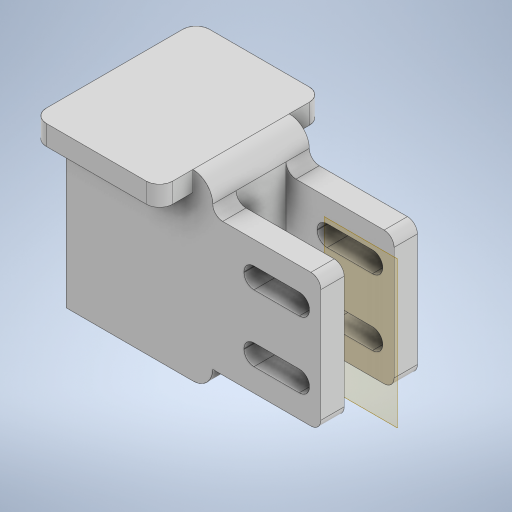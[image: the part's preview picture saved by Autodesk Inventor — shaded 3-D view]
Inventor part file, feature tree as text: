
AUTODESK INVENTOR PART (.ipt)
format: ipt  version: 2024 (Build 280153000, 153)  size: 822,784 bytes
history: native  units: mm
features: move_body x6, extrude x5, fillet x5, direct_edit x5, sketch x5, projected_geometry x5, other x2, plane x1, mirror x1, reference x1
ambient origin geometry x8: Origin, YZ Plane, XZ Plane, XY Plane, X Axis, Y Axis, Z Axis, Center Point
bodies: Solid1 (feature_tree)
feature tree (36):
  extrude  "Extrusion1"  Depth=20.0mm TaperAngle=0.0deg
  fillet  "Fillet1"  Radius=20.0mm
  plane  "Work Plane1"
  mirror  "Mirror1"
  fillet  "Fillet2"  [1 undecoded]
  extrude  "Extrusion2"  Depth=20.0mm
  fillet  "Fillet3"  Radius=10.0mm
  direct_edit  "Direct Edit1"
  extrude  "Extrusion3"  Depth=0.3mm
  direct_edit  "Direct Edit2"
  direct_edit  "Direct Edit3"
  direct_edit  "Direct Edit4"
  direct_edit  "Direct Edit5"
  extrude  "Extrusion4"  Depth=1.5mm
  fillet  "Fillet4"  Radius=1.5mm
  extrude  "Extrusion5"  Depth=20.0mm
  fillet  "Fillet5"  Radius=4.0mm
  sketch  "Sketch2"  dims[d0=40.0mm d1=4.0mm d2=0.0mm d5=20.0mm d6=0.0mm]
  reference  "Reference1"
  sketch  "Sketch3"  dims[d7=10.0mm d8=20.0mm d9=10.0mm]
  sketch  "Sketch4"  dims[d10=0.3mm d11=0.3mm]
  projected_geometry  "Projected Loop1"
  projected_geometry  "Projected Loop2"
  projected_geometry  "Projected Loop3"
  sketch  "Sketch5"  dims[d12=0.3mm d13=0.3mm d14=1.5mm]
  projected_geometry  "Projected Loop4"
  sketch  "Sketch6"  dims[d15=1.5mm d16=20.0mm d17=4.0mm d18=0.0mm d19=1.5mm d20=0.0mm d21=0.0mm d22=-0.5mm d23=3.0mm d24=0.0mm d25=0.0mm d26=0.0mm d27=-0.5mm d28=0.0mm d29=0.0mm d30=-0.5mm d31=0.0mm d32=0.0mm d33=-0.5mm d34=2.0mm d35=0.0mm d36=0.0mm d37=-0.5mm d38=0.0mm d39=0.0mm d40=2.0mm d41=25.25mm d42=0.0mm d43=8.0mm d44=3.0mm d45=5.0mm d46=5.0mm d47=3.0mm d48=0.0mm d49=2.0mm]
  projected_geometry  "Projected Loop5"
  other  "Assembly1"
  other  "micro-switch:1"
  move_body  "Move1"
  move_body  "Move2"
  move_body  "Move3"
  move_body  "Move4"
  move_body  "Move5"
  move_body  "Move6"
note: 1 required parameter value undecoded (feature->parameter linkage not recoverable at this tier; creation-order binding heuristic only, values carry confidence <= 0.55)
